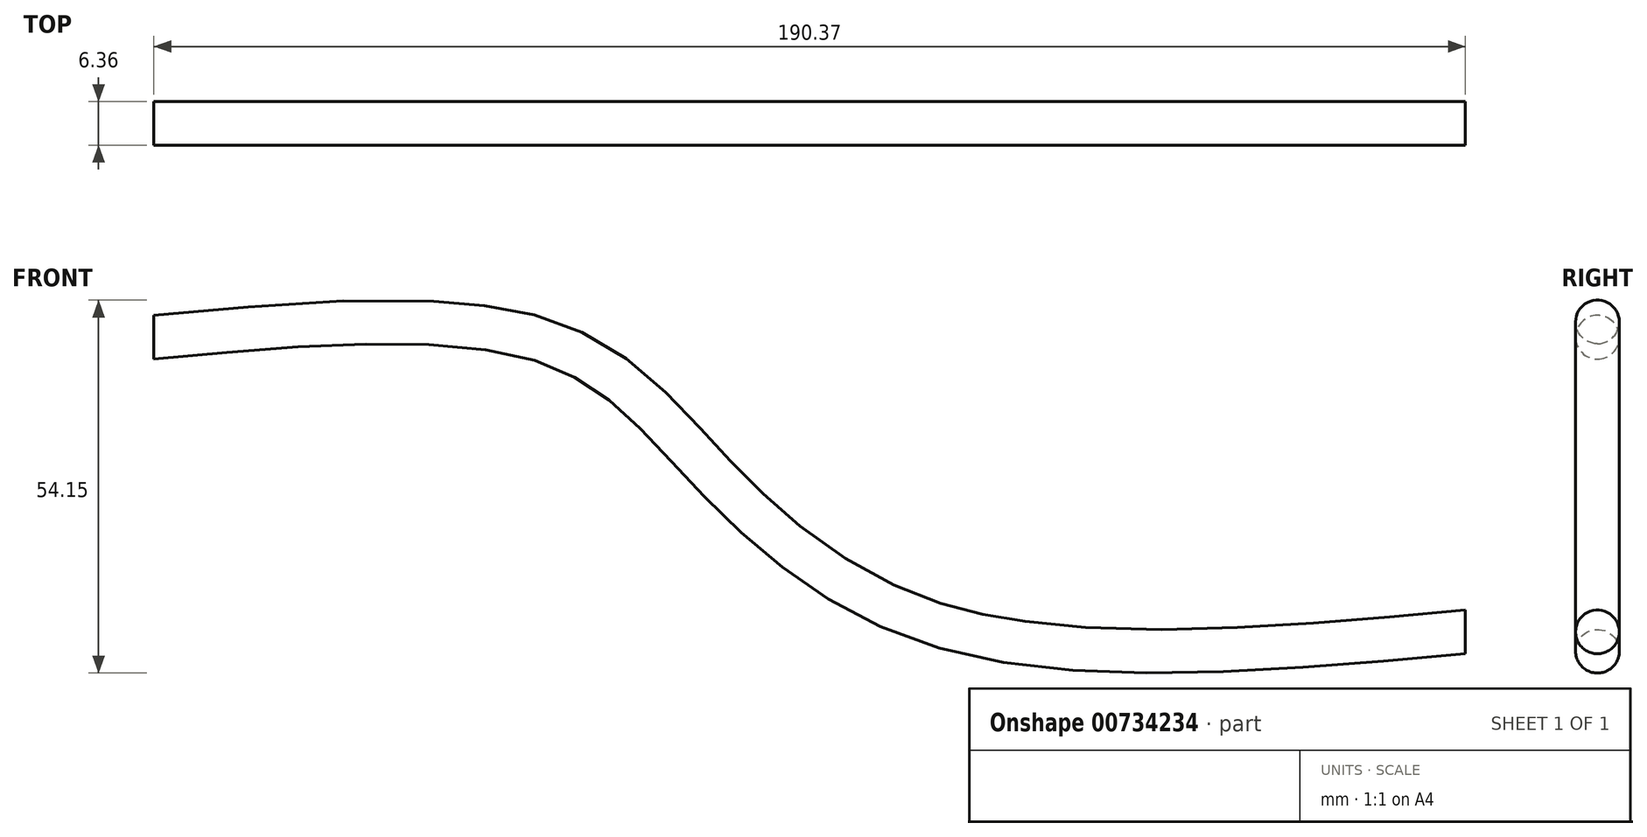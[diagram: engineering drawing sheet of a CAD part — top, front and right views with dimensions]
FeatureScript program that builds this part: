
annotation { "Feature Type Name" : "Feature", "Feature Type Description" : "" }
export const myFeature = defineFeature(function(context is Context, id is Id, definition is map)
    precondition{}
    {
        {
            var Q0;
            Q0=qCreatedBy(makeId("Front.planeOp"),FACE);
            var sketch = newSketch(context, id + "F0", { "sketchPlane" : qUnion([Q0])});
            skFitSpline(sketch, "E0", {"points": [v(-85.6, 23.11) * mm, v(-27.39, 22.08) * mm, v(-4.8, 3.6) * mm, v(28.07, -18.66) * mm, v(104.77, -19.69) * mm], "startDerivative": vector(244.77, 22.94) * mm, "endDerivative": vector(272.43, 24.95) * mm});
            skSolve(sketch);
        }
        {
            var Q0;
            Q0=qCreatedBy(makeId("Right.planeOp"),FACE);
            cPlane(context, id + "F1", {"entities" : qUnion([Q0]), "cplaneType" : CPlaneType.OFFSET, "offset" : 85.6 * mm, "oppositeDirection" : true, "width" : 152.4 * mm, "height" : 152.4 * mm});
        }
        {
            var Q0;
            Q0=qCreatedBy(id+"F1.planeOp",FACE);
            var sketch = newSketch(context, id + "F2", { "sketchPlane" : qUnion([Q0])});
            skPoint(sketch, "E1.0", {"position": v(0, 23.11) * mm});
            skCircle(sketch, "E2", {"center": v(0, 23.11) * mm, "radius": 3.18 * mm});
            skSolve(sketch);
        }
        {
            var Q0;
            Q0=makeQuery(id+"F2.imprint","IMPRINT",FACE,{"disambiguationData":[TD([[makeQuery(id+"F2.imprint","IMPRINT",EDGE,{"derivedFrom":sQuery(id+"F2.wireOp",EDGE,"E2")}),1.0]])]});
            var Q1;
            Q1=sQuery(id+"F0.wireOp",EDGE,"E0");
            sweep(context, id + "F3", {"profiles" : qUnion([Q0]), "path" : qUnion([Q1])});
        }
    });
